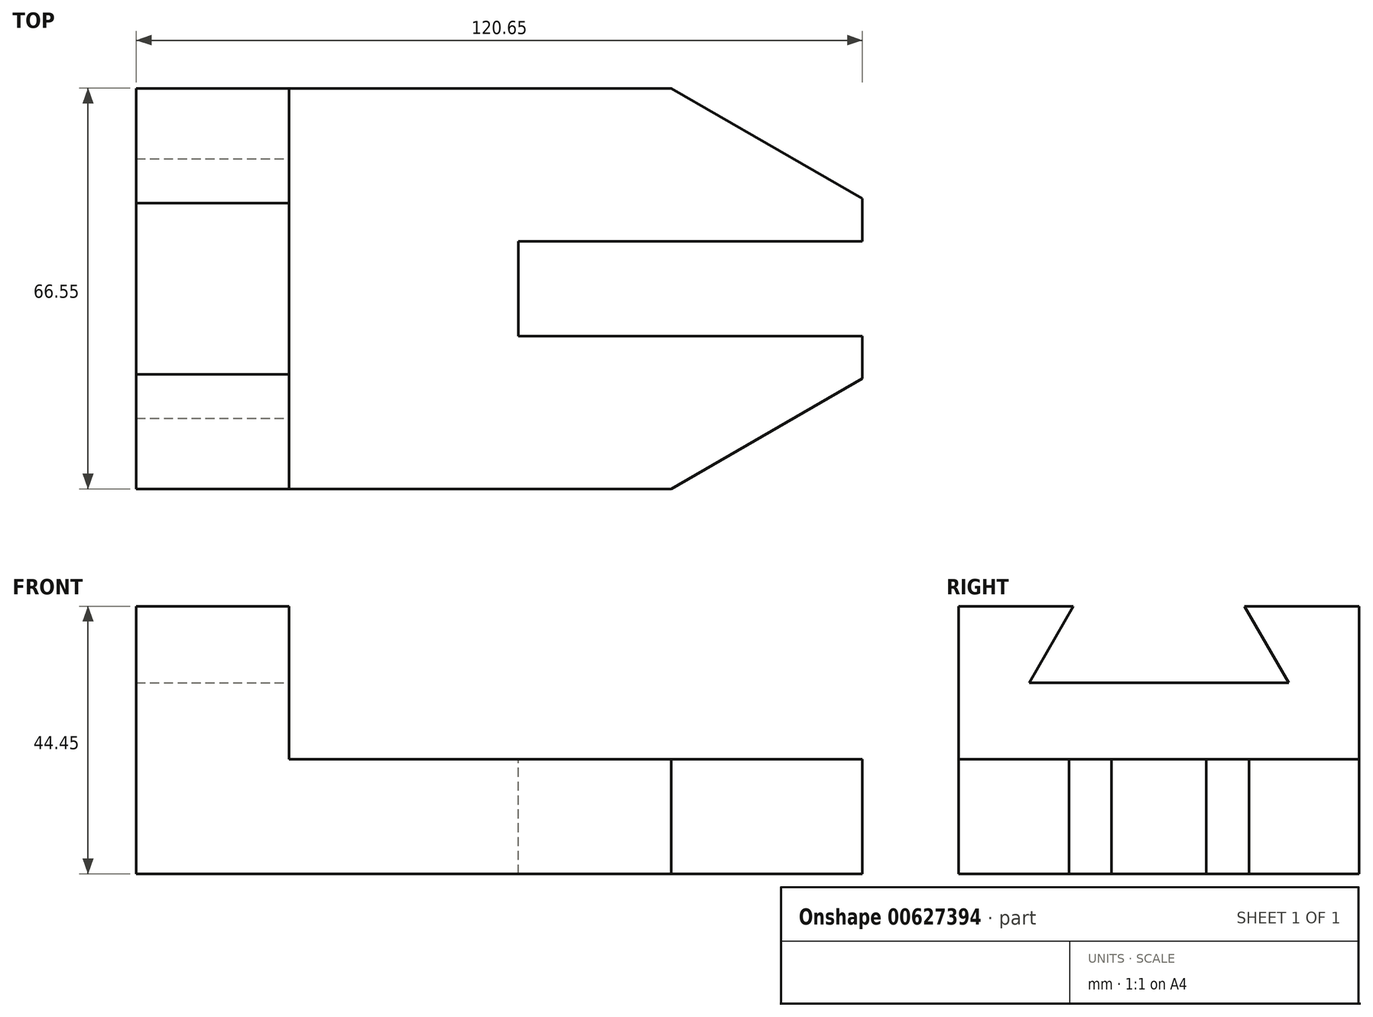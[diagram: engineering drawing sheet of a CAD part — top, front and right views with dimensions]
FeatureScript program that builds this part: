
annotation { "Feature Type Name" : "Feature", "Feature Type Description" : "" }
export const myFeature = defineFeature(function(context is Context, id is Id, definition is map)
    precondition{}
    {
        {
            var Q0;
            Q0=qCreatedBy(makeId("Top.planeOp"),FACE);
            var sketch = newSketch(context, id + "F0", { "sketchPlane" : qUnion([Q0])});
            skLineSegment(sketch, "E0.bottom", {"start": v(-51.48, -27.72) * mm, "end": v(69.17, -27.72) * mm});
            skLineSegment(sketch, "E0.top", {"start": v(-51.48, 38.83) * mm, "end": v(69.17, 38.83) * mm});
            skLineSegment(sketch, "E0.left", {"start": v(-51.48, -27.72) * mm, "end": v(-51.48, 38.83) * mm});
            skLineSegment(sketch, "E0.right", {"start": v(69.17, -27.72) * mm, "end": v(69.17, 38.83) * mm});
            skSolve(sketch);
        }
        {
            var Q0;
            Q0=makeQuery(id+"F0.imprint","IMPRINT",FACE,{"disambiguationData":[TD([[makeQuery(id+"F0.imprint","IMPRINT",EDGE,{"derivedFrom":sQuery(id+"F0.wireOp",EDGE,"E0.bottom")}),1.0]])]});
            extrude(context, id + "F1", {"entities" : qUnion([Q0]), "depth" : 44.45 * mm, "offsetDistance" : 25.4 * mm});
        }
        {
            var Q0;
            Q0=makeQuery(id+"F1.opExtrude","SWEPT_FACE",FACE,{"disambiguationData":[OSD([sQuery(id+"F0.wireOp",EDGE,"E0.bottom")])]});
            var sketch = newSketch(context, id + "F2", { "sketchPlane" : qUnion([Q0])});
            skLineSegment(sketch, "E1.bottom", {"start": v(69.17, 44.45) * mm, "end": v(-26.08, 44.45) * mm});
            skLineSegment(sketch, "E1.top", {"start": v(69.17, 19.05) * mm, "end": v(-26.08, 19.05) * mm});
            skLineSegment(sketch, "E1.left", {"start": v(69.17, 44.45) * mm, "end": v(69.17, 19.05) * mm});
            skLineSegment(sketch, "E1.right", {"start": v(-26.08, 44.45) * mm, "end": v(-26.08, 19.05) * mm});
            skSolve(sketch);
        }
        {
            var Q0;
            Q0=makeQuery(id+"F2.imprint","IMPRINT",FACE,{"disambiguationData":[TD([[makeQuery(id+"F2.imprint","IMPRINT",EDGE,{"derivedFrom":sQuery(id+"F2.wireOp",EDGE,"E1.bottom")}),-1.0]])]});
            extrude(context, id + "F3", {"entities" : qUnion([Q0]), "operationType" : NewBodyOperationType.REMOVE, "oppositeDirection" : true, "depth" : 182.37 * mm, "offsetDistance" : 25.4 * mm});
        }
        {
            var Q0;
            Q0=makeQuery(id+"F3.boolean.opBoolean","COPY",FACE,{"derivedFrom":makeQuery(id+"F3.opExtrude","SWEPT_FACE",FACE,{"disambiguationData":[OSD([sQuery(id+"F2.wireOp",EDGE,"E1.top")])]})});
            var sketch = newSketch(context, id + "F4", { "sketchPlane" : qUnion([Q0])});
            skLineSegment(sketch, "E2.top", {"start": v(69.17, 13.43) * mm, "end": v(12.02, 13.43) * mm});
            skLineSegment(sketch, "E2.left", {"start": v(69.17, 5.55) * mm, "end": v(69.17, 13.43) * mm});
            skLineSegment(sketch, "E2.right", {"start": v(12.02, 5.55) * mm, "end": v(12.02, 13.43) * mm});
            skLineSegment(sketch, "E3.MirrorCS", {"start": v(12.02, 5.55) * mm, "end": v(12.02, -2.32) * mm});
            skLineSegment(sketch, "E4.MirrorCS", {"start": v(69.17, -2.32) * mm, "end": v(12.02, -2.32) * mm});
            skLineSegment(sketch, "E5.MirrorCS", {"start": v(69.17, 5.55) * mm, "end": v(69.17, -2.32) * mm});
            skSolve(sketch);
        }
        {
            var Q0;
            Q0=makeQuery(id+"F4.imprint","IMPRINT",FACE,{"disambiguationData":[TD([[makeQuery(id+"F4.imprint","IMPRINT",EDGE,{"derivedFrom":sQuery(id+"F4.wireOp",EDGE,"E2.top")}),1.0]])]});
            extrude(context, id + "F5", {"entities" : qUnion([Q0]), "operationType" : NewBodyOperationType.REMOVE, "oppositeDirection" : true, "depth" : 80.52 * mm, "offsetDistance" : 25.4 * mm});
        }
        {
            var Q0;
            Q0=makeQuery(id+"F3.boolean.opBoolean","COPY",FACE,{"derivedFrom":makeQuery(id+"F3.opExtrude","SWEPT_FACE",FACE,{"disambiguationData":[OSD([sQuery(id+"F2.wireOp",EDGE,"E1.right")])]})});
            var sketch = newSketch(context, id + "F6", { "sketchPlane" : qUnion([Q0])});
            skLineSegment(sketch, "E6", {"start": v(-8.67, 44.45) * mm, "end": v(5.55, 44.45) * mm});
            skLineSegment(sketch, "E7", {"start": v(-8.67, 31.75) * mm, "end": v(5.55, 31.75) * mm});
            skLineSegment(sketch, "E8", {"start": v(-8.67, 31.75) * mm, "end": v(-16, 31.75) * mm});
            skLineSegment(sketch, "E9", {"start": v(-8.67, 44.45) * mm, "end": v(-16, 31.75) * mm});
            skPoint(sketch, "E10.orphan", {"position": v(-27.72, 31.75) * mm});
            skLineSegment(sketch, "E11.MirrorCS", {"start": v(19.78, 44.45) * mm, "end": v(5.55, 44.45) * mm});
            skLineSegment(sketch, "E12.MirrorCS", {"start": v(19.78, 44.45) * mm, "end": v(27.11, 31.75) * mm});
            skLineSegment(sketch, "E13.MirrorCS", {"start": v(19.78, 31.75) * mm, "end": v(27.11, 31.75) * mm});
            skLineSegment(sketch, "E14.MirrorCS", {"start": v(19.78, 31.75) * mm, "end": v(5.55, 31.75) * mm});
            skSolve(sketch);
        }
        {
            var Q0;
            Q0=makeQuery(id+"F6.imprint","IMPRINT",FACE,{"disambiguationData":[TD([[makeQuery(id+"F6.imprint","IMPRINT",EDGE,{"derivedFrom":sQuery(id+"F6.wireOp",EDGE,"E6")}),1.0]])]});
            extrude(context, id + "F7", {"entities" : qUnion([Q0]), "operationType" : NewBodyOperationType.REMOVE, "oppositeDirection" : true, "depth" : 103.63 * mm, "offsetDistance" : 25.4 * mm});
        }
        {
            var Q0;
            Q0=makeQuery(id+"F3.boolean.opBoolean","COPY",FACE,{"derivedFrom":makeQuery(id+"F3.opExtrude","SWEPT_FACE",FACE,{"disambiguationData":[OSD([sQuery(id+"F2.wireOp",EDGE,"E1.top")])]})});
            var sketch = newSketch(context, id + "F8", { "sketchPlane" : qUnion([Q0])});
            skLineSegment(sketch, "E15", {"start": v(69.17, 38.83) * mm, "end": v(37.42, 38.83) * mm});
            skLineSegment(sketch, "E16", {"start": v(37.42, 38.83) * mm, "end": v(69.17, 20.5) * mm});
            skLineSegment(sketch, "E17", {"start": v(69.17, -27.72) * mm, "end": v(37.42, -27.72) * mm});
            skLineSegment(sketch, "E18", {"start": v(37.42, -27.72) * mm, "end": v(69.17, -9.39) * mm});
            skLineSegment(sketch, "E19", {"start": v(69.17, 20.5) * mm, "end": v(69.17, 38.83) * mm});
            skLineSegment(sketch, "E20", {"start": v(69.17, -27.72) * mm, "end": v(69.17, -9.39) * mm});
            skSolve(sketch);
        }
        {
            var Q0;
            Q0=makeQuery(id+"F8.imprint","IMPRINT",FACE,{"disambiguationData":[TD([[makeQuery(id+"F8.imprint","IMPRINT",EDGE,{"derivedFrom":sQuery(id+"F8.wireOp",EDGE,"E17")}),-1.0]])]});
            var Q1;
            Q1=makeQuery(id+"F8.imprint","IMPRINT",FACE,{"disambiguationData":[TD([[makeQuery(id+"F8.imprint","IMPRINT",EDGE,{"derivedFrom":sQuery(id+"F8.wireOp",EDGE,"E15")}),-1.0]])]});
            extrude(context, id + "F9", {"entities" : qUnion([Q0, Q1]), "operationType" : NewBodyOperationType.REMOVE, "oppositeDirection" : true, "depth" : 44.2 * mm, "offsetDistance" : 25.4 * mm});
        }
    });
